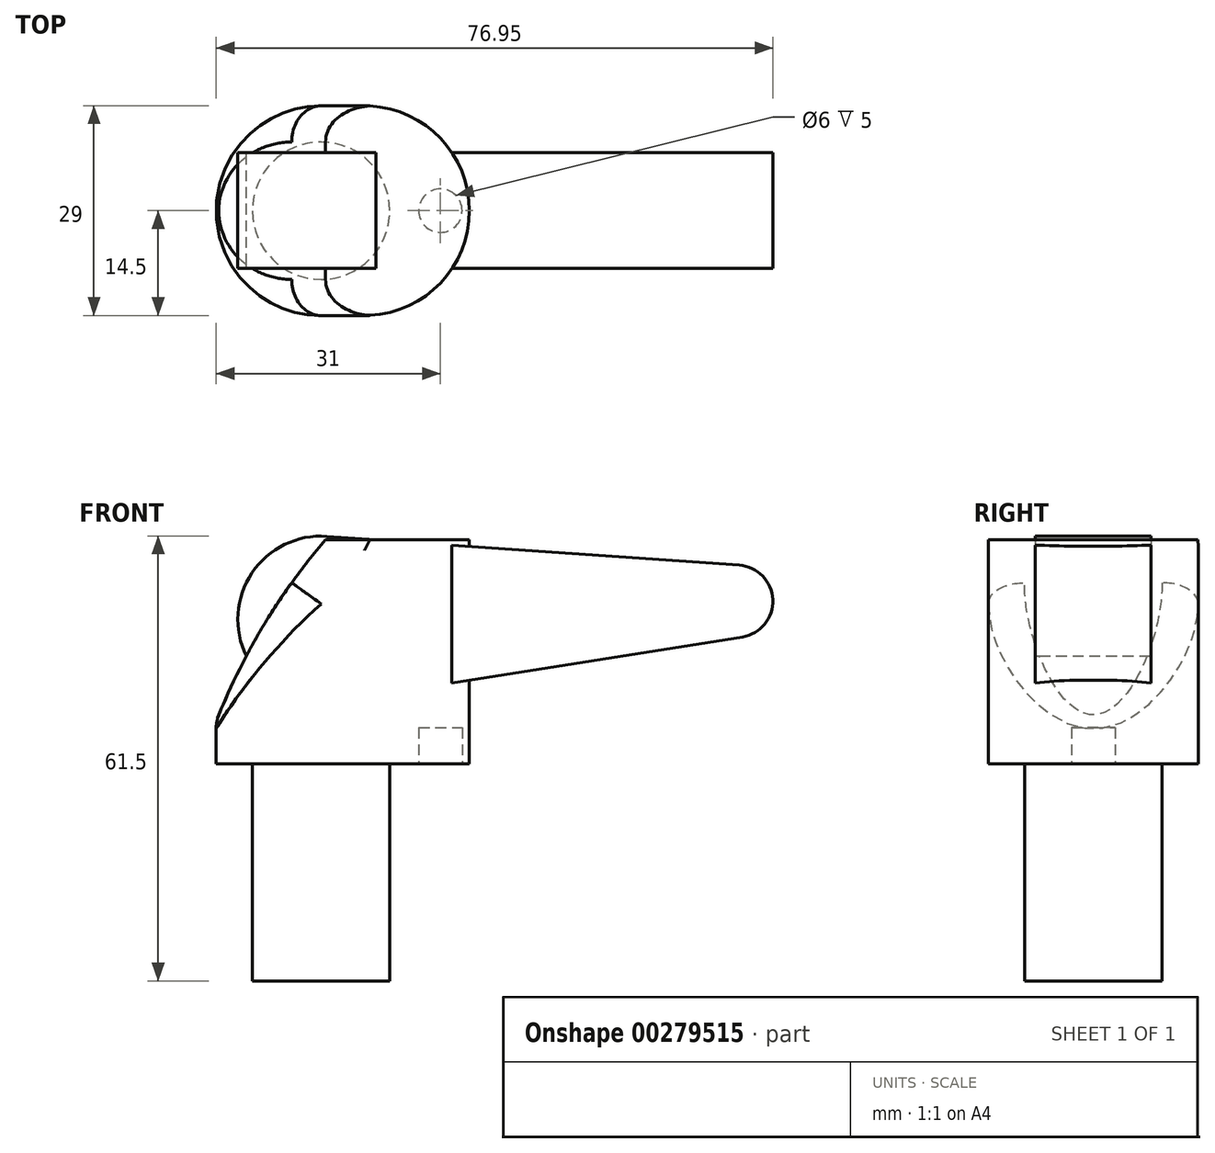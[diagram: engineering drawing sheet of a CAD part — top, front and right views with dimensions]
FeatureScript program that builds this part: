
annotation { "Feature Type Name" : "Feature", "Feature Type Description" : "" }
export const myFeature = defineFeature(function(context is Context, id is Id, definition is map)
    precondition{}
    {
        {
            var Q0;
            Q0=qCreatedBy(makeId("Top.planeOp"),FACE);
            var sketch = newSketch(context, id + "F0", { "sketchPlane" : qUnion([Q0])});
            skCircle(sketch, "E0", {"center": v(0, 0) * mm, "radius": 9.5 * mm});
            skSolve(sketch);
        }
        {
            var Q0;
            Q0=makeQuery(id+"F0.imprint","IMPRINT",FACE,{"disambiguationData":[TD([[makeQuery(id+"F0.imprint","IMPRINT",EDGE,{"derivedFrom":sQuery(id+"F0.wireOp",EDGE,"E0")}),1.0]])]});
            extrude(context, id + "F1", {"entities" : qUnion([Q0]), "depth" : 30 * mm});
        }
        {
            var Q0;
            Q0=makeQuery(id+"F1.opExtrude","CAP_FACE",FACE,{"disambiguationData":[OSD([sQuery(id+"F0.wireOp",EDGE,"E0")])],"isStart":false});
            var sketch = newSketch(context, id + "F2", { "sketchPlane" : qUnion([Q0])});
            skArc(sketch, "E1", {"start": v(0, 14.5) * mm, "mid": v(-14.5, 0) * mm, "end": v(0, -14.5) * mm});
            skArc(sketch, "E2", {"start": v(6, -14.5) * mm, "mid": v(20.5, 0) * mm, "end": v(6, 14.5) * mm});
            skLineSegment(sketch, "E3", {"start": v(0, 14.5) * mm, "end": v(6, 14.5) * mm});
            skLineSegment(sketch, "E4", {"start": v(0, -14.5) * mm, "end": v(6, -14.5) * mm});
            skSolve(sketch);
        }
        {
            var Q0;
            Q0 = qSketchRegion(id + "F2", true);
            extrude(context, id + "F3", {"entities" : qUnion([Q0]), "operationType" : NewBodyOperationType.ADD, "depth" : 31 * mm});
        }
        {
            var Q0;
            Q0=qCreatedBy(makeId("Front.planeOp"),FACE);
            var sketch = newSketch(context, id + "F4", { "sketchPlane" : qUnion([Q0])});
            skCircle(sketch, "E5", {"center": v(67, 4) * mm, "radius": 87.5 * mm, "construction": true});
            skLineSegment(sketch, "E6", {"start": v(-20.04, 13) * mm, "end": v(-48, 13) * mm});
            skLineSegment(sketch, "E7", {"start": v(-48, 13) * mm, "end": v(-48, 85) * mm});
            skLineSegment(sketch, "E8", {"start": v(-48, 85) * mm, "end": v(17, 85) * mm});
            skLineSegment(sketch, "E9", {"start": v(17, 85) * mm, "end": v(17, 75.8) * mm});
            skArc(sketch, "E10", {"start": v(-20.04, 13) * mm, "mid": v(-8.37, 48.45) * mm, "end": v(17, 75.8) * mm});
            skSolve(sketch);
        }
        {
            var Q0;
            Q0 = qSketchRegion(id + "F4", true);
            extrude(context, id + "F5", {"entities" : qUnion([Q0]), "operationType" : NewBodyOperationType.REMOVE, "endBound" : BoundingType.THROUGH_ALL, "oppositeDirection" : true, "depth" : 25 * mm, "hasSecondDirection" : true, "secondDirectionBound" : BoundingType.THROUGH_ALL, "secondDirectionOppositeDirection" : false, "secondDirectionDepth" : 25 * mm});
        }
        {
            var Q0;
            Q0=makeQuery(id+"F5.boolean.opBoolean","INTERSECT",EDGE,{"derivedFrom":[makeQuery(id+"F3.opExtrude","SWEPT_FACE",FACE,{"disambiguationData":[OSD([sQuery(id+"F2.wireOp",EDGE,"E1")])]}),makeQuery(id+"F5.opExtrude","SWEPT_FACE",FACE,{"disambiguationData":[OSD([sQuery(id+"F4.wireOp",EDGE,"E10")])]})]});
            fillet(context, id + "F6", {"entities" : qUnion([Q0]), "radius" : 5 * mm, "tangentPropagation" : true, "allowEdgeOverflow" : false});
        }
        {
            var Q0;
            Q0=qCreatedBy(makeId("Front.planeOp"),FACE);
            var sketch = newSketch(context, id + "F7", { "sketchPlane" : qUnion([Q0])});
            skArc(sketch, "E11", {"start": v(0.8, 61.47) * mm, "mid": v(-11.49, 49.5) * mm, "end": v(1.8, 38.64) * mm});
            skArc(sketch, "E12", {"start": v(58.23, 47.56) * mm, "mid": v(62.44, 52.72) * mm, "end": v(57.8, 57.49) * mm});
            skLineSegment(sketch, "E13", {"start": v(0, 50) * mm, "end": v(57.45, 52.5) * mm, "construction": true});
            skLineSegment(sketch, "E14", {"start": v(1.8, 38.64) * mm, "end": v(58.23, 47.56) * mm});
            skLineSegment(sketch, "E15", {"start": v(0.8, 61.47) * mm, "end": v(57.8, 57.49) * mm});
            skPoint(sketch, "E16.orphan", {"position": v(0, 38.36) * mm});
            skSolve(sketch);
        }
        {
            var Q0;
            Q0 = qSketchRegion(id + "F7", true);
            extrude(context, id + "F8", {"entities" : qUnion([Q0]), "operationType" : NewBodyOperationType.ADD, "depth" : 16 * mm, "symmetric" : true});
        }
        {
            var Q0;
            Q0=makeQuery(id+"F3.opExtrude","CAP_FACE",FACE,{"disambiguationData":[OSD([sQuery(id+"F2.wireOp",EDGE,"E1"),sQuery(id+"F2.wireOp",EDGE,"E2"),sQuery(id+"F2.wireOp",EDGE,"E3"),sQuery(id+"F2.wireOp",EDGE,"E4")])],"isStart":true});
            var sketch = newSketch(context, id + "F9", { "sketchPlane" : qUnion([Q0])});
            skCircle(sketch, "E17", {"center": v(16.5, 0) * mm, "radius": 3 * mm});
            skSolve(sketch);
        }
        {
            var Q0;
            Q0=makeQuery(id+"F9.imprint","IMPRINT",FACE,{"disambiguationData":[TD([[makeQuery(id+"F9.imprint","IMPRINT",EDGE,{"derivedFrom":sQuery(id+"F9.wireOp",EDGE,"E17")}),1.0]])]});
            var Q1;
            Q1=sQuery(id+"F9.wireOp",EDGE,"E17");
            extrude(context, id + "F10", {"entities" : qUnion([Q0]), "operationType" : NewBodyOperationType.REMOVE, "surfaceEntities" : qUnion([Q1]), "oppositeDirection" : true, "depth" : 5 * mm});
        }
    });
